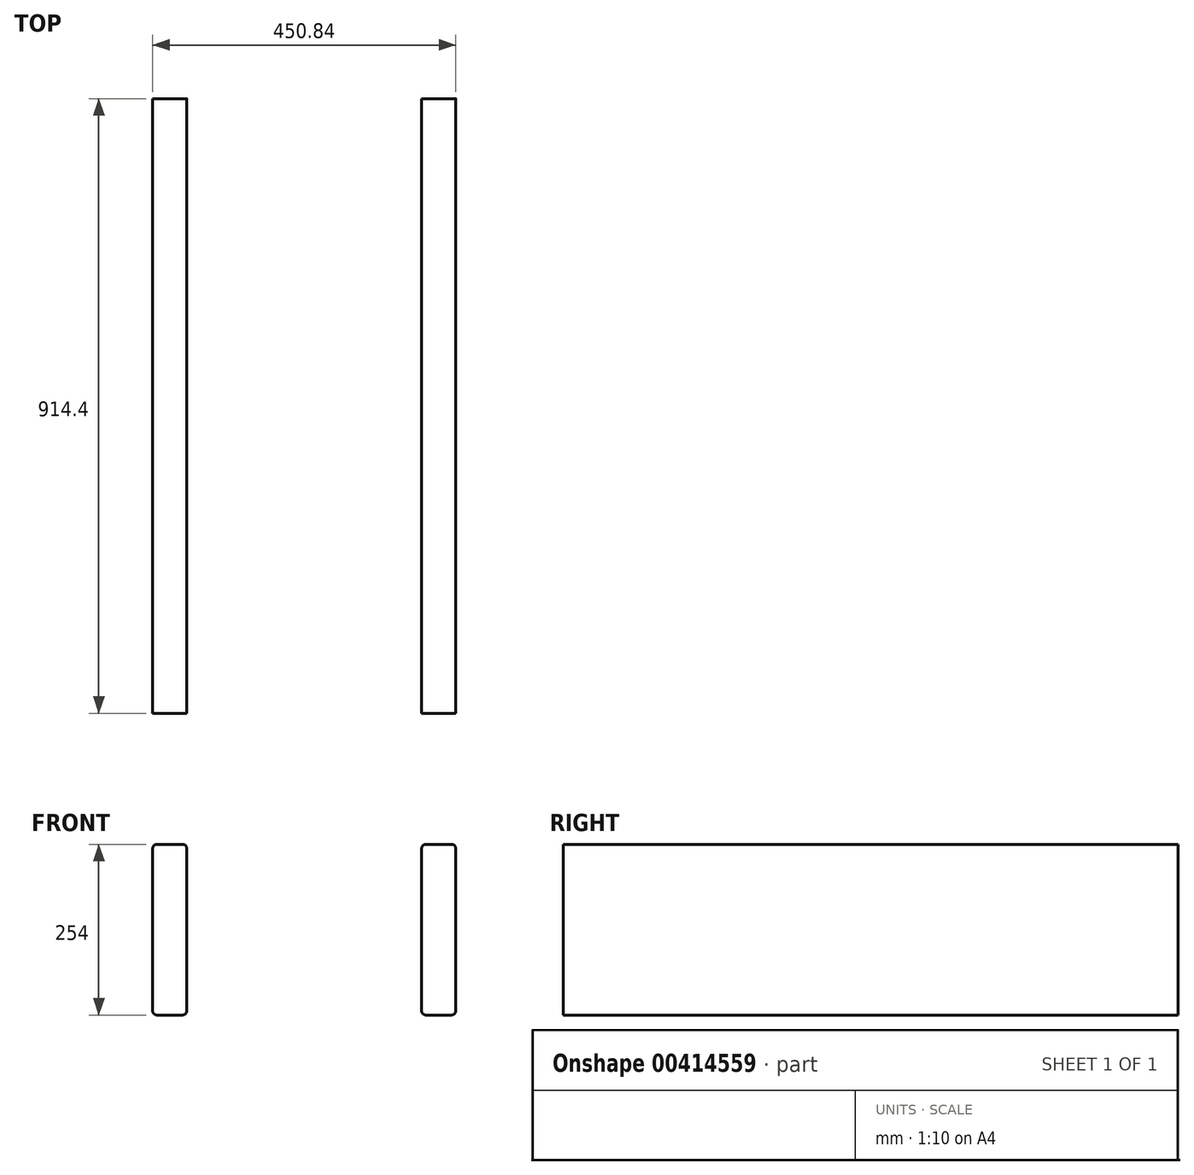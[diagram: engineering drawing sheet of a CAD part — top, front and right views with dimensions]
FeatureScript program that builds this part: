
annotation { "Feature Type Name" : "Feature", "Feature Type Description" : "" }
export const myFeature = defineFeature(function(context is Context, id is Id, definition is map)
    precondition{}
    {
        {
            var Q0;
            Q0=qCreatedBy(makeId("Front.planeOp"),FACE);
            var sketch = newSketch(context, id + "F0", { "sketchPlane" : qUnion([Q0])});
            skLineSegment(sketch, "E0.bottom", {"start": v(-174.63, 0) * mm, "end": v(-225.43, 0) * mm});
            skLineSegment(sketch, "E0.top", {"start": v(-174.63, 254) * mm, "end": v(-225.43, 254) * mm});
            skLineSegment(sketch, "E0.left", {"start": v(-174.63, 0) * mm, "end": v(-174.63, 254) * mm});
            skLineSegment(sketch, "E0.right", {"start": v(-225.43, 0) * mm, "end": v(-225.43, 254) * mm});
            skLineSegment(sketch, "E1.bottom", {"start": v(174.63, 0) * mm, "end": v(225.43, 0) * mm});
            skLineSegment(sketch, "E1.top", {"start": v(174.62, 254) * mm, "end": v(225.42, 254) * mm});
            skLineSegment(sketch, "E1.left", {"start": v(174.63, 0) * mm, "end": v(174.62, 254) * mm});
            skLineSegment(sketch, "E1.right", {"start": v(225.43, 0) * mm, "end": v(225.42, 254) * mm});
            skSolve(sketch);
        }
        {
            var Q0;
            Q0 = qSketchRegion(id + "F0", true);
            extrude(context, id + "F1", {"entities" : qUnion([Q0]), "depth" : 914.4 * mm});
        }
        {
            var Q0;
            Q0=makeQuery(id+"F1.opExtrude","SWEPT_EDGE",EDGE,{"disambiguationData":[OSD([sQuery(id+"F0.wireOp",EDGE,"E0.top"),sQuery(id+"F0.wireOp",EDGE,"E0.left")])]});
            var Q1;
            Q1=makeQuery(id+"F1.opExtrude","SWEPT_EDGE",EDGE,{"disambiguationData":[OSD([sQuery(id+"F0.wireOp",EDGE,"E0.top"),sQuery(id+"F0.wireOp",EDGE,"E0.right")])]});
            var Q2;
            Q2=makeQuery(id+"F1.opExtrude","SWEPT_EDGE",EDGE,{"disambiguationData":[OSD([sQuery(id+"F0.wireOp",EDGE,"E0.bottom"),sQuery(id+"F0.wireOp",EDGE,"E0.left")])]});
            var Q3;
            Q3=makeQuery(id+"F1.opExtrude","SWEPT_EDGE",EDGE,{"disambiguationData":[OSD([sQuery(id+"F0.wireOp",EDGE,"E0.bottom"),sQuery(id+"F0.wireOp",EDGE,"E0.right")])]});
            var Q4;
            Q4=makeQuery(id+"F1.opExtrude","SWEPT_EDGE",EDGE,{"disambiguationData":[OSD([sQuery(id+"F0.wireOp",EDGE,"E1.top"),sQuery(id+"F0.wireOp",EDGE,"E1.left")])]});
            var Q5;
            Q5=makeQuery(id+"F1.opExtrude","SWEPT_EDGE",EDGE,{"disambiguationData":[OSD([sQuery(id+"F0.wireOp",EDGE,"E1.top"),sQuery(id+"F0.wireOp",EDGE,"E1.right")])]});
            var Q6;
            Q6=makeQuery(id+"F1.opExtrude","SWEPT_EDGE",EDGE,{"disambiguationData":[OSD([sQuery(id+"F0.wireOp",EDGE,"E1.bottom"),sQuery(id+"F0.wireOp",EDGE,"E1.right")])]});
            var Q7;
            Q7=makeQuery(id+"F1.opExtrude","SWEPT_EDGE",EDGE,{"disambiguationData":[OSD([sQuery(id+"F0.wireOp",EDGE,"E1.bottom"),sQuery(id+"F0.wireOp",EDGE,"E1.left")])]});
            fillet(context, id + "F2", {"entities" : qUnion([Q0, Q1, Q2, Q3, Q4, Q5, Q6, Q7]), "radius" : 6.35 * mm, "tangentPropagation" : true, "allowEdgeOverflow" : false});
        }
    });
